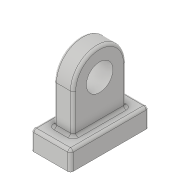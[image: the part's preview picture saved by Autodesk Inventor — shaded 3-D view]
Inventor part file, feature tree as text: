
AUTODESK INVENTOR PART (.ipt)
format: ipt  version: 2017 (Build 210142000, 142)  size: 155,136 bytes
history: native  units: in
note: dims shown in document units (in); Inventor stores cm internally (conversion verified against a paired STEP export)
features: fillet x4, extrude x2, sketch x2
ambient origin geometry x8: Origin, YZ Plane, XZ Plane, XY Plane, X Axis, Y Axis, Z Axis, Center Point
bodies: Solid1 (feature_tree)
feature tree (8):
  extrude  "Extrusion1"  Depth=0.59in
  extrude  "Extrusion2"  Depth=0.59in
  fillet  "Fillet1"  Radius=0.4in
  fillet  "Fillet2"  Radius=0.4in
  fillet  "Fillet3"  Radius=0.4in
  fillet  "Fillet4"  Radius=0.29in
  sketch  "Sketch1"  dims[d0=1.18in d1=0.59in]
  sketch  "Sketch2"  dims[d2=0.29in d3=0.0in d4=0.59in d5=0.4in d6=0.4in d7=0.4in d8=0.29in d9=0.0in d10=0.04in d11=0.04in d12=0.04in d13=0.04in]
